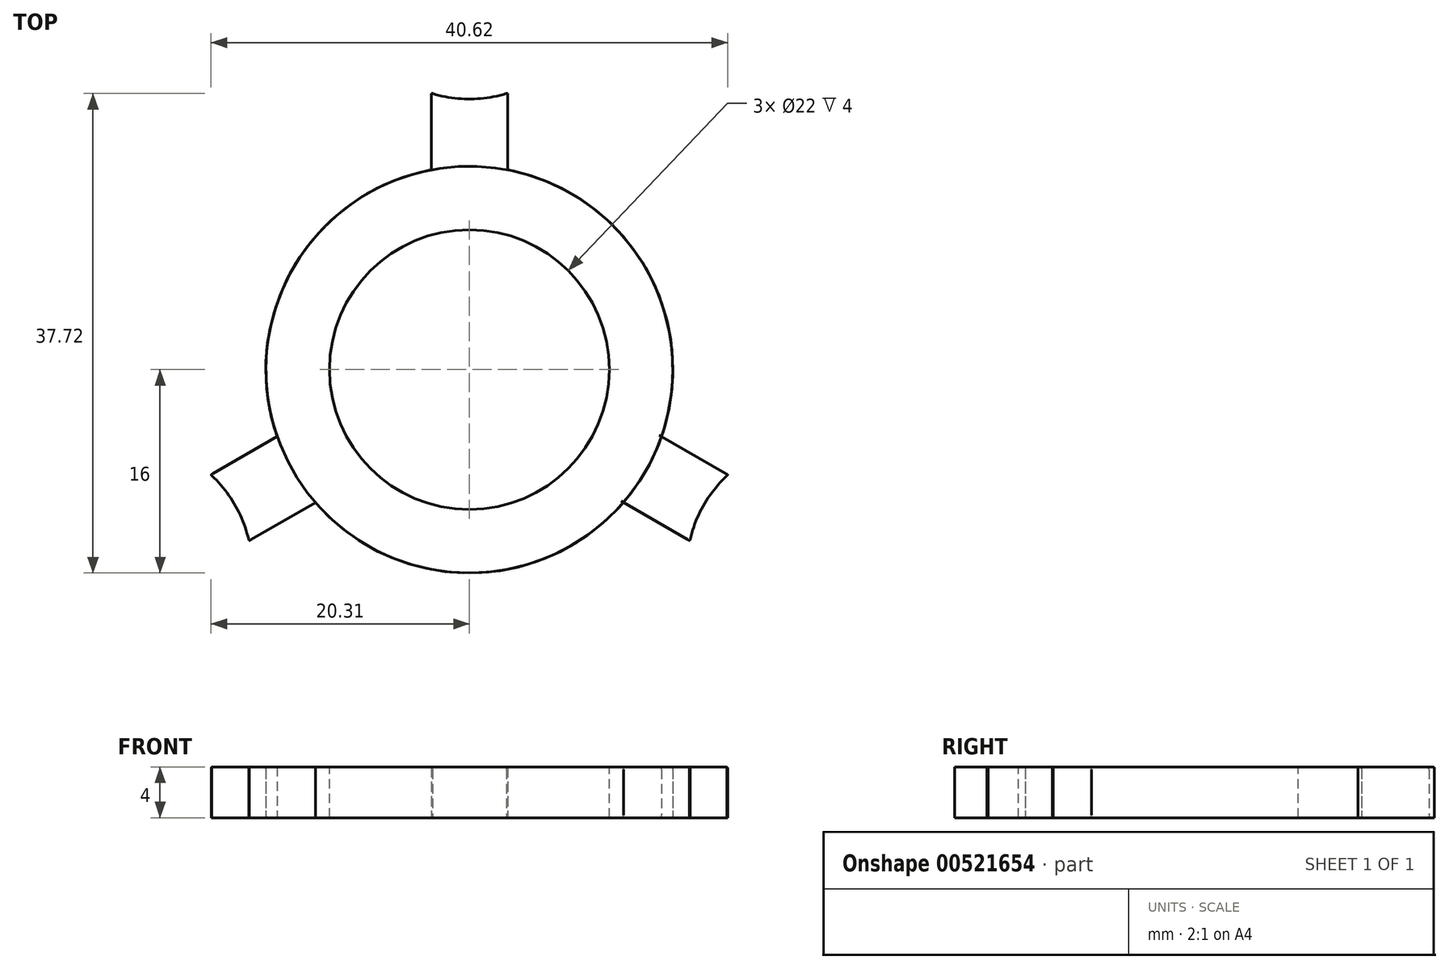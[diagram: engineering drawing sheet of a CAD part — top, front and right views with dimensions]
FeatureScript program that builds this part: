
annotation { "Feature Type Name" : "Feature", "Feature Type Description" : "" }
export const myFeature = defineFeature(function(context is Context, id is Id, definition is map)
    precondition{}
    {
        {
            var Q0;
            Q0=qCreatedBy(makeId("Top.planeOp"),FACE);
            var sketch = newSketch(context, id + "F0", { "sketchPlane" : qUnion([Q0])});
            skCircle(sketch, "E0", {"center": v(0, 0) * mm, "radius": 16 * mm});
            skLineSegment(sketch, "E1", {"start": v(-3, 15.72) * mm, "end": v(-3, 21.72) * mm});
            skLineSegment(sketch, "E2", {"start": v(-3, 21.72) * mm, "end": v(3, 21.72) * mm});
            skLineSegment(sketch, "E3", {"start": v(3, 21.72) * mm, "end": v(3, 15.72) * mm});
            skCircle(sketch, "E4", {"center": v(0, 31.28) * mm, "radius": 10 * mm});
            skSolve(sketch);
        }
        {
            var Q0;
            {var subQ0=sQuery(id+"F0.wireOp",EDGE,"E0");var subQ1=makeQuery(id+"F0.imprint","INTERSECT",VERTEX,{"derivedFrom":[subQ0,sQuery(id+"F0.wireOp",EDGE,"E1")]});Q0=makeQuery(id+"F0.imprint","IMPRINT",FACE,{"disambiguationData":[TD([[makeQuery(id+"F0.imprint","IMPRINT",EDGE,{"disambiguationData":[TD([[subQ1,1.0]])],"derivedFrom":subQ0}),1.0]])]});}
            var Q1;
            {var subQ1=sQuery(id+"F0.wireOp",EDGE,"E1");Q1=makeQuery(id+"F0.imprint","IMPRINT",FACE,{"disambiguationData":[TD([[makeQuery(id+"F0.imprint","IMPRINT",EDGE,{"derivedFrom":subQ1}),-1.0]])]});}
            var Q2;
            {var subQ0=sQuery(id+"F0.wireOp",EDGE,"E4");var subQ1=sQuery(id+"F0.wireOp",EDGE,"E2");var subQ2=makeQuery(id+"F0.imprint","INTERSECT",VERTEX,{"disambiguationData":[OD(0.0)],"derivedFrom":[subQ1,subQ0]});Q2=makeQuery(id+"F0.imprint","IMPRINT",FACE,{"disambiguationData":[TD([[makeQuery(id+"F0.imprint","IMPRINT",EDGE,{"disambiguationData":[TD([[subQ2,-1.0]])],"derivedFrom":subQ1}),-1.0]])]});}
            var Q3;
            {var subQ0=sQuery(id+"F0.wireOp",EDGE,"E4");var subQ1=sQuery(id+"F0.wireOp",EDGE,"E2");var subQ2=makeQuery(id+"F0.imprint","INTERSECT",VERTEX,{"disambiguationData":[OD(0.0)],"derivedFrom":[subQ1,subQ0]});Q3=makeQuery(id+"F0.imprint","IMPRINT",FACE,{"disambiguationData":[TD([[makeQuery(id+"F0.imprint","IMPRINT",EDGE,{"disambiguationData":[TD([[subQ2,-1.0]])],"derivedFrom":subQ1}),1.0]])]});}
            extrude(context, id + "F1", {"entities" : qUnion([Q0, Q1, Q2, Q3]), "depth" : 4 * mm, "offsetDistance" : 25 * mm});
        }
        {
            var Q0;
            Q0=makeQuery(id+"F1.opExtrude","CAP_FACE",FACE,{"disambiguationData":[OSD([sQuery(id+"F0.wireOp",EDGE,"E0"),sQuery(id+"F0.wireOp",EDGE,"E1"),sQuery(id+"F0.wireOp",EDGE,"E2"),sQuery(id+"F0.wireOp",EDGE,"E3"),sQuery(id+"F0.wireOp",EDGE,"E4")])],"isStart":false});
            var sketch = newSketch(context, id + "F2", { "sketchPlane" : qUnion([Q0])});
            skCircle(sketch, "E5", {"center": v(0, 31.28) * mm, "radius": 9 * mm});
            skSolve(sketch);
        }
        {
            var Q0;
            Q0 = qSketchRegion(id + "F2", true);
            extrude(context, id + "F3", {"entities" : qUnion([Q0]), "operationType" : NewBodyOperationType.REMOVE, "oppositeDirection" : true, "depth" : 25 * mm, "offsetDistance" : 25 * mm});
        }
        {
            var Q0;
            Q0=makeQuery(id+"F1.opExtrude","SWEPT_BODY",BODY,{"disambiguationData":[OSD([sQuery(id+"F0.wireOp",EDGE,"E0"),sQuery(id+"F0.wireOp",EDGE,"E1"),sQuery(id+"F0.wireOp",EDGE,"E2"),sQuery(id+"F0.wireOp",EDGE,"E3"),sQuery(id+"F0.wireOp",EDGE,"E4")])]});
            var Q1;
            Q1=makeQuery(id+"F1.opExtrude","SWEPT_FACE",FACE,{"disambiguationData":[OSD([sQuery(id+"F0.wireOp",EDGE,"E0")])]});
            circularPattern(context, id + "F4", {"entities" : qUnion([Q0]), "axis" : qUnion([Q1]), "angle" : 360 * degree, "instanceCount" : 3, "equalSpace" : true});
        }
        {
            var Q0;
            Q0=makeQuery(id+"F1.opExtrude","CAP_FACE",FACE,{"disambiguationData":[OSD([sQuery(id+"F0.wireOp",EDGE,"E0"),sQuery(id+"F0.wireOp",EDGE,"E1"),sQuery(id+"F0.wireOp",EDGE,"E2"),sQuery(id+"F0.wireOp",EDGE,"E3"),sQuery(id+"F0.wireOp",EDGE,"E4")])],"isStart":false});
            var sketch = newSketch(context, id + "F5", { "sketchPlane" : qUnion([Q0])});
            skCircle(sketch, "E6", {"center": v(0, 0) * mm, "radius": 11 * mm});
            skSolve(sketch);
        }
        {
            var Q0;
            Q0 = qSketchRegion(id + "F5", true);
            extrude(context, id + "F6", {"entities" : qUnion([Q0]), "operationType" : NewBodyOperationType.REMOVE, "endBound" : BoundingType.THROUGH_ALL, "oppositeDirection" : true, "depth" : 25 * mm, "offsetDistance" : 25 * mm});
        }
        {
            var Q0;
            Q0=makeQuery(id+"F4.opPattern","COPY",EDGE,{"derivedFrom":makeQuery(id+"F1.opExtrude","CAP_EDGE",EDGE,{"disambiguationData":[OSD([sQuery(id+"F0.wireOp",EDGE,"E4")])],"isStart":false}),"instanceName":"2"});
            var Q1;
            Q1=makeQuery(id+"F4.opPattern","COPY",EDGE,{"derivedFrom":makeQuery(id+"F1.opExtrude","CAP_EDGE",EDGE,{"disambiguationData":[OSD([sQuery(id+"F0.wireOp",EDGE,"E0")])],"isStart":false}),"instanceName":"1"});
            var Q2;
            Q2=makeQuery(id+"F4.opPattern","COPY",EDGE,{"derivedFrom":makeQuery(id+"F1.opExtrude","CAP_EDGE",EDGE,{"disambiguationData":[OSD([sQuery(id+"F0.wireOp",EDGE,"E0")])],"isStart":true}),"instanceName":"1"});
            var Q3;
            Q3=makeQuery(id+"F4.opPattern","COPY",EDGE,{"derivedFrom":makeQuery(id+"F1.opExtrude","CAP_EDGE",EDGE,{"disambiguationData":[OSD([sQuery(id+"F0.wireOp",EDGE,"E4")])],"isStart":false}),"instanceName":"1"});
            var Q4;
            Q4=makeQuery(id+"F1.opExtrude","CAP_EDGE",EDGE,{"disambiguationData":[OSD([sQuery(id+"F0.wireOp",EDGE,"E4")])],"isStart":false});
            fillet(context, id + "F7", {"entities" : qUnion([Q0, Q1, Q2, Q3, Q4]), "radius" : .2 * mm, "tangentPropagation" : true, "rho" : 0.5, "crossSection" : FilletCrossSection.CONIC, "allowEdgeOverflow" : false});
        }
    });
